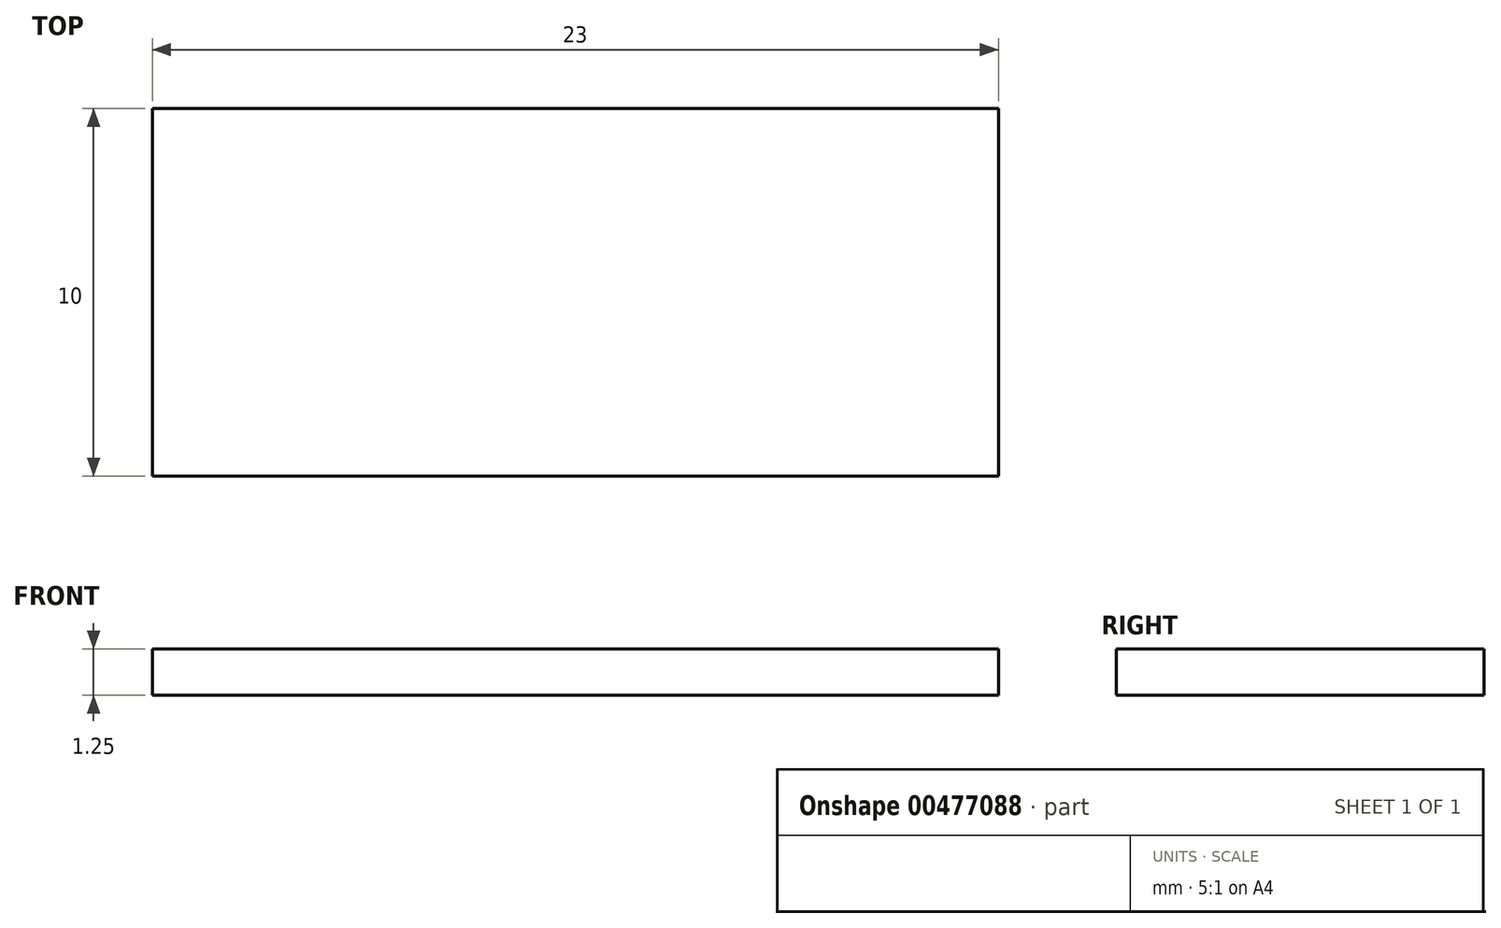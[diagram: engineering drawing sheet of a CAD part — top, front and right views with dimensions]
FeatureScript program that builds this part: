
annotation { "Feature Type Name" : "Feature", "Feature Type Description" : "" }
export const myFeature = defineFeature(function(context is Context, id is Id, definition is map)
    precondition{}
    {
        {
            var Q0;
            Q0=qCreatedBy(makeId("Top.planeOp"),FACE);
            var sketch = newSketch(context, id + "F0", { "sketchPlane" : qUnion([Q0])});
            skLineSegment(sketch, "E0.bottom", {"start": v(-49.98, -4.76) * mm, "end": v(-26.98, -4.76) * mm});
            skLineSegment(sketch, "E0.top", {"start": v(-49.98, -14.76) * mm, "end": v(-26.98, -14.76) * mm});
            skLineSegment(sketch, "E0.left", {"start": v(-49.98, -4.76) * mm, "end": v(-49.98, -14.76) * mm});
            skLineSegment(sketch, "E0.right", {"start": v(-26.98, -4.76) * mm, "end": v(-26.98, -14.76) * mm});
            skSolve(sketch);
        }
        {
            var Q0;
            Q0=qSketchRegion(id+"F0",true);
            extrude(context, id + "F1", {"entities" : qUnion([Q0]), "depth" : 1.25 * mm});
        }
    });
